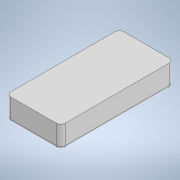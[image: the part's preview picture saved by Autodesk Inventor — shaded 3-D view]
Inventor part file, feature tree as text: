
AUTODESK INVENTOR PART (.ipt)
format: ipt  version: 2020 (Build 240168000, 168)  size: 107,520 bytes
history: native  units: in
note: dims shown in document units (in); Inventor stores cm internally (conversion verified against a paired STEP export)
features: extrude x1, fillet x1, sketch x1
ambient origin geometry x8: Origin, YZ Plane, XZ Plane, XY Plane, X Axis, Y Axis, Z Axis, Center Point
bodies: Solid1 (feature_tree)
feature tree (3):
  extrude  "Extrusion1"  Depth=1.5in
  fillet  "Fillet1"  Radius=0.6in
  sketch  "Sketch1"  dims[d0=3.115in d1=1.5in d2=0.6in d3=0.0in d4=0.0625in d5=0.125in]
